# Revit family: Haworth_Mex-Hi_Sofa_OneArm
name_source: partatom
category: Furniture
revit_build: Autodesk Revit 2018 (Build: 20170223_1515(x64)
units: mm (PartAtom-declared; Revit-internal decimal feet)

## family parameters
Always vertical = Yes
Cut with Voids When Loaded = No
OmniClass Number = 23.40.70.14.64.21
OmniClass Title = Systems Furniture
Room Calculation Point = No
Shared = No
Work Plane-Based = No

## types (2) — shared parameters
Actual Depth = 35.5 "
Actual Height = 28.3 "
Assembly Code = E2020200
Manufacturer = Haworth
Model = HCCSMHL
Revision Number = 1
Size = Verify Final Dim. w/ Haworth
Sustainability Info = https://www.haworth.com
Trim Finish = Haworth _ Polymer _ Black
URL = https://www.haworth.com
URL - Product = https://www.haworth.com
Warranty = http://www.haworth.com

## per-type parameters (varying)
| type | Actual Width | Description | Three Seats | Two Seats |
| Three Seat Sofa | 98.4 " | Haworth - Cassina - Mex-Hi - Sofa - With One Arm - Three Seat | Yes | No |
| Two Seat Sofa | 70.9 " | Haworth - Cassina - Mex-Hi - Sofa - With One Arm - Wide Two Seat | No | Yes |

## geometry (parser evidence)
native form markers: Sweep x17
no freeform markers — native parametric forms only
